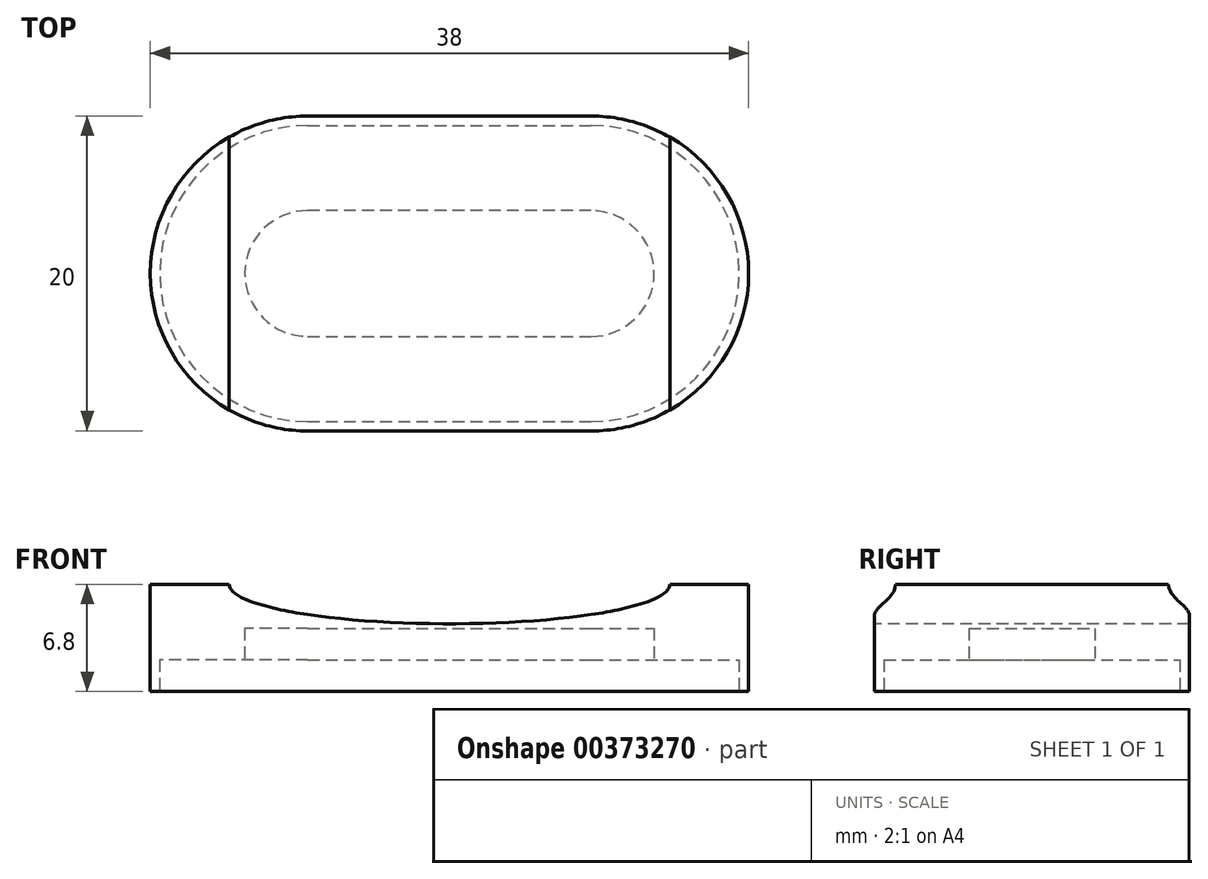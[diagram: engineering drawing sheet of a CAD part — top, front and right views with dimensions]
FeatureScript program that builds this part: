
annotation { "Feature Type Name" : "Feature", "Feature Type Description" : "" }
export const myFeature = defineFeature(function(context is Context, id is Id, definition is map)
    precondition{}
    {
        {
            var Q0;
            Q0=qCreatedBy(makeId("Top.planeOp"),FACE);
            var sketch = newSketch(context, id + "F0", { "sketchPlane" : qUnion([Q0])});
            skLineSegment(sketch, "E0", {"start": v(-56.54, 0.05) * mm, "end": v(-18.54, 0.05) * mm});
            skLineSegment(sketch, "E1", {"start": v(-37.54, 0.05) * mm, "end": v(-37.54, 10.05) * mm});
            skLineSegment(sketch, "E2", {"start": v(-37.54, 0.05) * mm, "end": v(-37.54, -9.95) * mm});
            skArc(sketch, "E3", {"start": v(-28.54, -9.95) * mm, "mid": v(-18.54, 0.05) * mm, "end": v(-28.54, 10.05) * mm});
            skArc(sketch, "E4", {"start": v(-46.54, 10.05) * mm, "mid": v(-56.54, 0.05) * mm, "end": v(-46.54, -9.95) * mm});
            skLineSegment(sketch, "E5", {"start": v(-46.54, 10.05) * mm, "end": v(-28.54, 10.05) * mm});
            skLineSegment(sketch, "E6.MirrorCS", {"start": v(-46.54, -9.95) * mm, "end": v(-28.54, -9.95) * mm});
            skSolve(sketch);
        }
        {
            var Q0;
            Q0 = qSketchRegion(id + "F0", true);
            extrude(context, id + "F1", {"entities" : qUnion([Q0]), "depth" : 6.8 * mm});
        }
        {
            var Q0;
            Q0=makeQuery(id+"F1.opExtrude","SWEPT_FACE",FACE,{"disambiguationData":[OSD([sQuery(id+"F0.wireOp",EDGE,"E6.MirrorCS")])]});
            var sketch = newSketch(context, id + "F2", { "sketchPlane" : qUnion([Q0])});
            skEllipse(sketch, "E7", {"center": v(-37.54, 6.8) * mm, "majorRadius": 14 * mm, "minorRadius": 2.5 * mm, "majorAxis": v(1, 0)});
            skSolve(sketch);
        }
        {
            var Q0;
            {var subQ1=sQuery(id+"F0.wireOp",EDGE,"E6.MirrorCS");var subQ6=makeQuery(id+"F1.opExtrude","CAP_EDGE",EDGE,{"disambiguationData":[OSD([subQ1])],"isStart":false});Q0=makeQuery(id+"F2.imprint","IMPRINT",FACE,{"disambiguationData":[TD([[makeQuery(id+"F2.imprint","IMPRINT",EDGE,{"derivedFrom":subQ6}),1.0]])]});}
            var Q1;
            {var subQ1=sQuery(id+"F0.wireOp",EDGE,"E6.MirrorCS");var subQ6=makeQuery(id+"F1.opExtrude","CAP_EDGE",EDGE,{"disambiguationData":[OSD([subQ1])],"isStart":false});Q1=makeQuery(id+"F2.imprint","IMPRINT",FACE,{"disambiguationData":[TD([[makeQuery(id+"F2.imprint","IMPRINT",EDGE,{"derivedFrom":subQ6}),-1.0]])]});}
            var Q2;
            Q2=sQuery(id+"F2.wireOp",EDGE,"E7");
            extrude(context, id + "F3", {"entities" : qUnion([Q0, Q1]), "operationType" : NewBodyOperationType.REMOVE, "surfaceEntities" : qUnion([Q2]), "oppositeDirection" : true, "depth" : 25 * mm});
        }
        {
            var Q0;
            Q0=makeQuery(id+"F1.opExtrude","CAP_FACE",FACE,{"disambiguationData":[OSD([sQuery(id+"F0.wireOp",EDGE,"E3"),sQuery(id+"F0.wireOp",EDGE,"E4"),sQuery(id+"F0.wireOp",EDGE,"E5"),sQuery(id+"F0.wireOp",EDGE,"E6.MirrorCS")])],"isStart":true});
            var sketch = newSketch(context, id + "F4", { "sketchPlane" : qUnion([Q0])});
            skLineSegment(sketch, "E8.0", {"start": v(-46.54, 9.95) * mm, "end": v(-28.54, 9.95) * mm});
            skArc(sketch, "E8.1", {"start": v(-28.54, 9.95) * mm, "mid": v(-18.54, -0.05) * mm, "end": v(-28.54, -10.05) * mm});
            skLineSegment(sketch, "E8.2", {"start": v(-46.54, -10.05) * mm, "end": v(-28.54, -10.05) * mm});
            skArc(sketch, "E8.3", {"start": v(-46.54, -10.05) * mm, "mid": v(-56.54, -0.05) * mm, "end": v(-46.54, 9.95) * mm});
            skLineSegment(sketch, "E9.0", {"start": v(-46.54, 9.35) * mm, "end": v(-28.54, 9.35) * mm});
            skArc(sketch, "E9.1", {"start": v(-46.54, -9.45) * mm, "mid": v(-55.94, -0.05) * mm, "end": v(-46.54, 9.35) * mm});
            skLineSegment(sketch, "E9.2", {"start": v(-46.54, -9.45) * mm, "end": v(-28.54, -9.45) * mm});
            skArc(sketch, "E9.3", {"start": v(-28.54, 9.35) * mm, "mid": v(-19.14, -0.05) * mm, "end": v(-28.54, -9.45) * mm});
            skSolve(sketch);
        }
        {
            var Q0;
            Q0=makeQuery(id+"F4.imprint","IMPRINT",FACE,{"disambiguationData":[TD([[makeQuery(id+"F4.imprint","IMPRINT",EDGE,{"derivedFrom":sQuery(id+"F4.wireOp",EDGE,"E9.0")}),-1.0]])]});
            extrude(context, id + "F5", {"entities" : qUnion([Q0]), "operationType" : NewBodyOperationType.REMOVE, "oppositeDirection" : true, "depth" : 2 * mm});
        }
        {
            var Q0;
            Q0=makeQuery(id+"F5.boolean.opBoolean","COPY",FACE,{"derivedFrom":makeQuery(id+"F5.opExtrude","CAP_FACE",FACE,{"disambiguationData":[OSD([sQuery(id+"F4.wireOp",EDGE,"E9.0"),sQuery(id+"F4.wireOp",EDGE,"E9.1"),sQuery(id+"F4.wireOp",EDGE,"E9.2"),sQuery(id+"F4.wireOp",EDGE,"E9.3")])],"isStart":false})});
            var sketch = newSketch(context, id + "F6", { "sketchPlane" : qUnion([Q0])});
            skArc(sketch, "E10", {"start": v(-46.54, 3.95) * mm, "mid": v(-50.54, -0.05) * mm, "end": v(-46.54, -4.05) * mm});
            skArc(sketch, "E11", {"start": v(-28.54, -4.05) * mm, "mid": v(-24.54, -0.05) * mm, "end": v(-28.54, 3.95) * mm});
            skLineSegment(sketch, "E12", {"start": v(-46.54, 3.95) * mm, "end": v(-28.54, 3.95) * mm});
            skLineSegment(sketch, "E13", {"start": v(-28.54, -4.05) * mm, "end": v(-46.54, -4.05) * mm});
            skSolve(sketch);
        }
        {
            var Q0;
            Q0=makeQuery(id+"F6.imprint","IMPRINT",FACE,{"disambiguationData":[TD([[makeQuery(id+"F6.imprint","IMPRINT",EDGE,{"derivedFrom":sQuery(id+"F6.wireOp",EDGE,"E10")}),1.0]])]});
            extrude(context, id + "F7", {"entities" : qUnion([Q0]), "operationType" : NewBodyOperationType.REMOVE, "oppositeDirection" : true, "depth" : 2 * mm});
        }
    });
